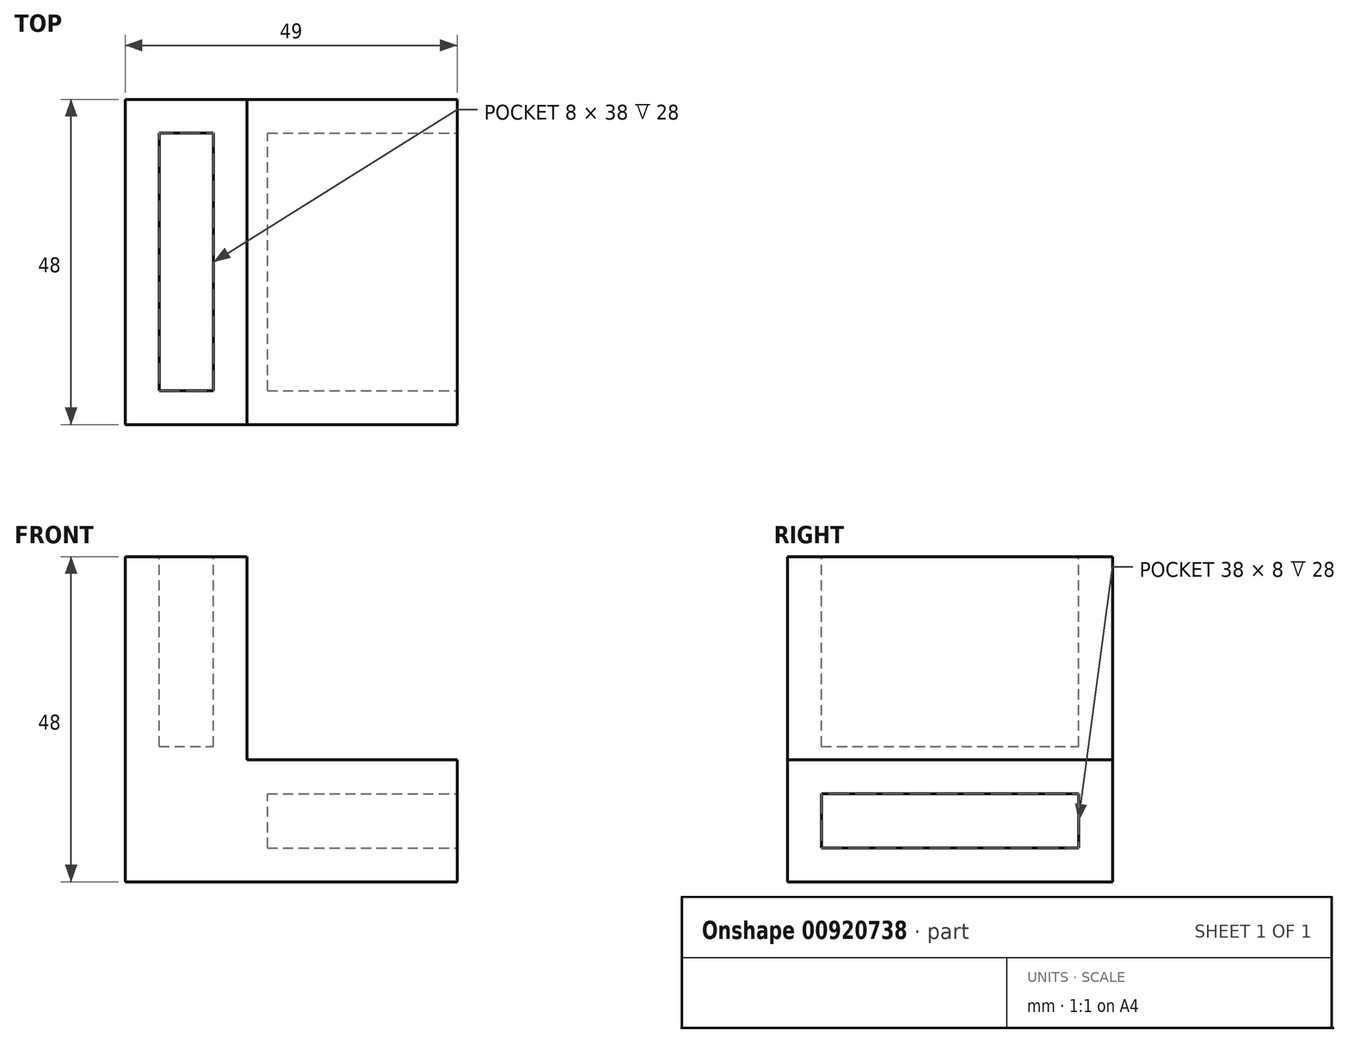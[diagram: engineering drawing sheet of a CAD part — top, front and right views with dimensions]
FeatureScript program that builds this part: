
annotation { "Feature Type Name" : "Feature", "Feature Type Description" : "" }
export const myFeature = defineFeature(function(context is Context, id is Id, definition is map)
    precondition{}
    {
        {
            var Q0;
            Q0=qCreatedBy(makeId("Top.planeOp"),FACE);
            var sketch = newSketch(context, id + "F0", { "sketchPlane" : qUnion([Q0])});
            skLineSegment(sketch, "E0.bottom", {"start": v(0, 0) * mm, "end": v(-49, 0) * mm});
            skLineSegment(sketch, "E0.top", {"start": v(0, 48) * mm, "end": v(-49, 48) * mm});
            skLineSegment(sketch, "E0.left", {"start": v(0, 0) * mm, "end": v(0, 48) * mm});
            skLineSegment(sketch, "E0.right", {"start": v(-49, 0) * mm, "end": v(-49, 48) * mm});
            skSolve(sketch);
        }
        {
            var Q0;
            Q0 = qSketchRegion(id + "F0", true);
            extrude(context, id + "F1", {"entities" : qUnion([Q0]), "depth" : 18 * mm, "offsetDistance" : 25 * mm});
        }
        {
            var Q0;
            Q0=makeQuery(id+"F1.opExtrude","SWEPT_FACE",FACE,{"disambiguationData":[OSD([sQuery(id+"F0.wireOp",EDGE,"E0.left")])]});
            var sketch = newSketch(context, id + "F2", { "sketchPlane" : qUnion([Q0])});
            skLineSegment(sketch, "E1.bottom", {"start": v(5, 5) * mm, "end": v(43, 5) * mm});
            skLineSegment(sketch, "E1.top", {"start": v(5, 13) * mm, "end": v(43, 13) * mm});
            skLineSegment(sketch, "E1.left", {"start": v(5, 5) * mm, "end": v(5, 13) * mm});
            skLineSegment(sketch, "E1.right", {"start": v(43, 5) * mm, "end": v(43, 13) * mm});
            skSolve(sketch);
        }
        {
            var Q0;
            Q0=makeQuery(id+"F2.imprint","IMPRINT",FACE,{"disambiguationData":[TD([[makeQuery(id+"F2.imprint","IMPRINT",EDGE,{"derivedFrom":sQuery(id+"F2.wireOp",EDGE,"E1.bottom")}),1.0]])]});
            extrude(context, id + "F3", {"entities" : qUnion([Q0]), "operationType" : NewBodyOperationType.REMOVE, "oppositeDirection" : true, "depth" : 28 * mm, "offsetDistance" : 25 * mm});
        }
        {
            var Q0;
            Q0=makeQuery(id+"F1.opExtrude","CAP_FACE",FACE,{"disambiguationData":[OSD([sQuery(id+"F0.wireOp",EDGE,"E0.bottom"),sQuery(id+"F0.wireOp",EDGE,"E0.top"),sQuery(id+"F0.wireOp",EDGE,"E0.left"),sQuery(id+"F0.wireOp",EDGE,"E0.right")])],"isStart":false});
            var sketch = newSketch(context, id + "F4", { "sketchPlane" : qUnion([Q0])});
            skLineSegment(sketch, "E2.bottom", {"start": v(-49, 0) * mm, "end": v(-31, 0) * mm});
            skLineSegment(sketch, "E2.top", {"start": v(-49, 48) * mm, "end": v(-31, 48) * mm});
            skLineSegment(sketch, "E2.left", {"start": v(-49, 0) * mm, "end": v(-49, 48) * mm});
            skLineSegment(sketch, "E2.right", {"start": v(-31, 0) * mm, "end": v(-31, 48) * mm});
            skSolve(sketch);
        }
        {
            var Q0;
            Q0=makeQuery(id+"F4.imprint","IMPRINT",FACE,{"disambiguationData":[TD([[makeQuery(id+"F4.imprint","IMPRINT",EDGE,{"derivedFrom":sQuery(id+"F4.wireOp",EDGE,"E2.bottom")}),-1.0]])]});
            extrude(context, id + "F5", {"entities" : qUnion([Q0]), "operationType" : NewBodyOperationType.ADD, "depth" : 30 * mm, "offsetDistance" : 25 * mm});
        }
        {
            var Q0;
            Q0=makeQuery(id+"F5.opExtrude","CAP_FACE",FACE,{"disambiguationData":[OSD([sQuery(id+"F4.wireOp",EDGE,"E2.bottom"),sQuery(id+"F4.wireOp",EDGE,"E2.top"),sQuery(id+"F4.wireOp",EDGE,"E2.left"),sQuery(id+"F4.wireOp",EDGE,"E2.right")])],"isStart":false});
            var sketch = newSketch(context, id + "F6", { "sketchPlane" : qUnion([Q0])});
            skLineSegment(sketch, "E3.bottom", {"start": v(-44, 5) * mm, "end": v(-36, 5) * mm});
            skLineSegment(sketch, "E3.top", {"start": v(-44, 43) * mm, "end": v(-36, 43) * mm});
            skLineSegment(sketch, "E3.left", {"start": v(-44, 5) * mm, "end": v(-44, 43) * mm});
            skLineSegment(sketch, "E3.right", {"start": v(-36, 5) * mm, "end": v(-36, 43) * mm});
            skSolve(sketch);
        }
        {
            var Q0;
            Q0=makeQuery(id+"F6.imprint","IMPRINT",FACE,{"disambiguationData":[TD([[makeQuery(id+"F6.imprint","IMPRINT",EDGE,{"derivedFrom":sQuery(id+"F6.wireOp",EDGE,"E3.bottom")}),1.0]])]});
            extrude(context, id + "F7", {"entities" : qUnion([Q0]), "operationType" : NewBodyOperationType.REMOVE, "oppositeDirection" : true, "depth" : 28 * mm, "offsetDistance" : 25 * mm});
        }
    });
